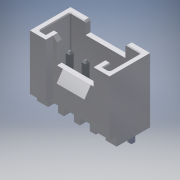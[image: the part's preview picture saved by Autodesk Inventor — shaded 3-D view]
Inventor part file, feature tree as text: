
AUTODESK INVENTOR PART (.ipt)
format: ipt  version: 2019.4 (Build 234330000, 330)  size: 364,544 bytes
history: mixed  units: mm
features: projected_geometry x8, sketch x5, extrude x2, other x1, mirror x1, sweep x1, imported_body x1
ambient origin geometry x8: Origin, YZ Plane, XZ Plane, XY Plane, X Axis, Y Axis, Z Axis, Center Point
bodies: Solide1 (imported_parasolid)
feature tree (19):
  other  "Chanfrein5"
  mirror  "Symétrie1"
  sketch  "Esquisse2"
  sketch  "Esquisse3"
  extrude  "Extrusion2"  Depth=1.2mm TaperAngle=0.0deg
  extrude  "Extrusion3"  TaperAngle=0.0deg  [1 undecoded]
  sweep  "Balayage1"
  projected_geometry  "Boucle projetée1"
  sketch  "Esquisse4"
  projected_geometry  "Boucle projetée2"
  projected_geometry  "Boucle projetée3"
  projected_geometry  "Boucle projetée4"
  projected_geometry  "Boucle projetée5"
  sketch  "Esquisse5"
  projected_geometry  "Boucle projetée6"
  projected_geometry  "Boucle projetée7"
  projected_geometry  "Boucle projetée8"
  sketch  "Esquisse6"
  imported_body  NMx_Import_Brep_tag  [imported B-rep: ~159 faces, bbox_mm=[10.0, 10.512254, 5.1]]
note: 1 required parameter value undecoded (feature->parameter linkage not recoverable at this tier; creation-order binding heuristic only, values carry confidence <= 0.55)
